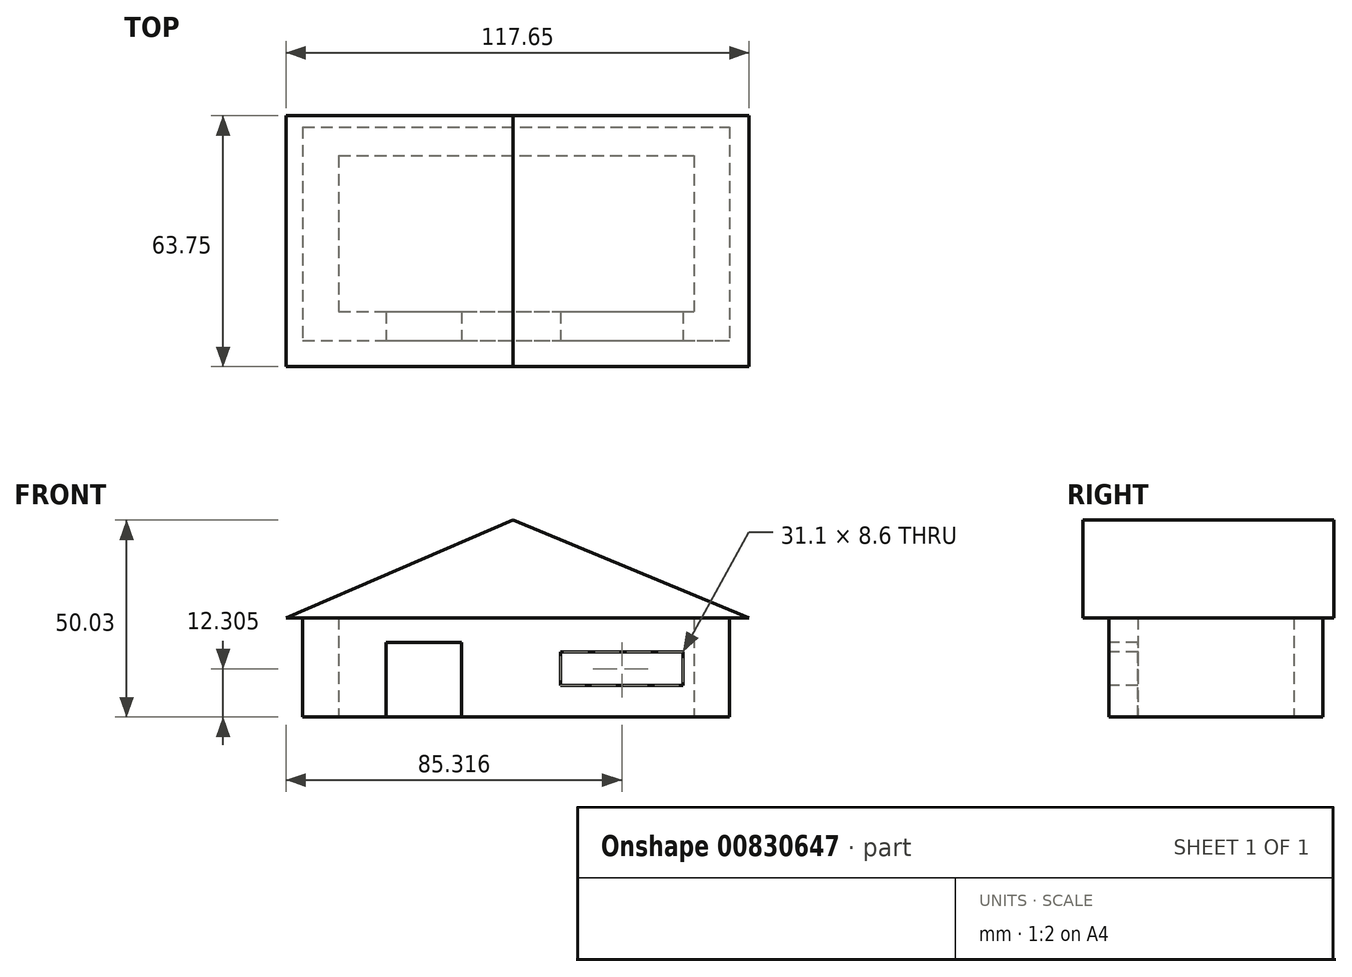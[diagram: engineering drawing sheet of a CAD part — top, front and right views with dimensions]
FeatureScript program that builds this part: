
annotation { "Feature Type Name" : "Feature", "Feature Type Description" : "" }
export const myFeature = defineFeature(function(context is Context, id is Id, definition is map)
    precondition{}
    {
        {
            var Q0;
            Q0=qCreatedBy(makeId("Top.planeOp"),FACE);
            var sketch = newSketch(context, id + "F0", { "sketchPlane" : qUnion([Q0])});
            skLineSegment(sketch, "E0.bottom", {"start": v(-45.13, 19.8) * mm, "end": v(45.13, 19.8) * mm});
            skLineSegment(sketch, "E0.top", {"start": v(-45.13, -19.8) * mm, "end": v(45.13, -19.8) * mm});
            skLineSegment(sketch, "E0.left", {"start": v(-45.13, 19.8) * mm, "end": v(-45.13, -19.8) * mm});
            skLineSegment(sketch, "E0.right", {"start": v(45.13, 19.8) * mm, "end": v(45.13, -19.8) * mm});
            skPoint(sketch, "E0.middle", {"position": v(0, 0) * mm});
            skLineSegment(sketch, "E1.bottom", {"start": v(-54.2, 27.15) * mm, "end": v(54.2, 27.15) * mm});
            skLineSegment(sketch, "E1.top", {"start": v(-54.2, -27.15) * mm, "end": v(54.2, -27.15) * mm});
            skLineSegment(sketch, "E1.left", {"start": v(-54.2, 27.15) * mm, "end": v(-54.2, -27.15) * mm});
            skLineSegment(sketch, "E1.right", {"start": v(54.2, 27.15) * mm, "end": v(54.2, -27.15) * mm});
            skLineSegment(sketch, "E2.bottom", {"start": v(-28.23, 27.15) * mm, "end": v(-10.51, 27.15) * mm});
            skLineSegment(sketch, "E2.top", {"start": v(-28.23, 19.8) * mm, "end": v(-10.51, 19.8) * mm});
            skLineSegment(sketch, "E2.left", {"start": v(-28.23, 27.15) * mm, "end": v(-28.23, 19.8) * mm});
            skLineSegment(sketch, "E2.right", {"start": v(-10.51, 27.15) * mm, "end": v(-10.51, 19.8) * mm});
            skSolve(sketch);
        }
        {
            var Q0;
            {var subQ2=sQuery(id+"F0.wireOp",EDGE,"E2.left");Q0=makeQuery(id+"F0.imprint","IMPRINT",FACE,{"disambiguationData":[TD([[makeQuery(id+"F0.imprint","IMPRINT",EDGE,{"derivedFrom":subQ2}),1.0]])]});}
            var Q1;
            Q1=makeQuery(id+"F0.imprint","IMPRINT",FACE,{"disambiguationData":[TD([[makeQuery(id+"F0.imprint","IMPRINT",EDGE,{"derivedFrom":sQuery(id+"F0.wireOp",EDGE,"E0.top")}),-1.0]])]});
            extrude(context, id + "F1", {"entities" : qUnion([Q0, Q1]), "depth" : 25.4 * mm, "offsetDistance" : 25.4 * mm});
        }
        {
            var Q0;
            Q0=makeQuery(id+"F1.opExtrude","SWEPT_FACE",FACE,{"disambiguationData":[OSD([sQuery(id+"F0.wireOp",EDGE,"E1.top")])]});
            var sketch = newSketch(context, id + "F2", { "sketchPlane" : qUnion([Q0])});
            skLineSegment(sketch, "E3.bottom", {"start": v(-33, 0) * mm, "end": v(-13.84, 0) * mm});
            skLineSegment(sketch, "E3.top", {"start": v(-33, 19) * mm, "end": v(-13.84, 19) * mm});
            skLineSegment(sketch, "E3.left", {"start": v(-33, 0) * mm, "end": v(-33, 19) * mm});
            skLineSegment(sketch, "E3.right", {"start": v(-13.84, 0) * mm, "end": v(-13.84, 19) * mm});
            skLineSegment(sketch, "E4.bottom", {"start": v(14, 19.1) * mm, "end": v(39.13, 19.1) * mm});
            skLineSegment(sketch, "E4.top", {"start": v(14, 8.94) * mm, "end": v(39.13, 8.94) * mm});
            skLineSegment(sketch, "E4.left", {"start": v(14, 19.1) * mm, "end": v(14, 8.94) * mm});
            skLineSegment(sketch, "E4.right", {"start": v(39.13, 19.1) * mm, "end": v(39.13, 8.94) * mm});
            skSolve(sketch);
        }
        {
            var Q0;
            Q0=makeQuery(id+"F2.imprint","IMPRINT",FACE,{"disambiguationData":[TD([[makeQuery(id+"F2.imprint","IMPRINT",EDGE,{"derivedFrom":sQuery(id+"F2.wireOp",EDGE,"E3.bottom")}),1.0]])]});
            extrude(context, id + "F3", {"entities" : qUnion([Q0]), "operationType" : NewBodyOperationType.REMOVE, "endBound" : BoundingType.UP_TO_NEXT, "oppositeDirection" : true, "depth" : 25.4 * mm, "offsetDistance" : 25.4 * mm});
        }
        {
            var Q0;
            Q0=makeQuery(id+"F1.opExtrude","SWEPT_FACE",FACE,{"disambiguationData":[OSD([sQuery(id+"F0.wireOp",EDGE,"E1.top")])]});
            var sketch = newSketch(context, id + "F4", { "sketchPlane" : qUnion([Q0])});
            skLineSegment(sketch, "E5.bottom", {"start": v(14.6, 17.68) * mm, "end": v(40.3, 17.68) * mm});
            skLineSegment(sketch, "E5.top", {"start": v(14.6, 7.44) * mm, "end": v(40.3, 7.44) * mm});
            skLineSegment(sketch, "E5.left", {"start": v(14.6, 17.68) * mm, "end": v(14.6, 7.44) * mm});
            skLineSegment(sketch, "E5.right", {"start": v(40.3, 17.68) * mm, "end": v(40.3, 7.44) * mm});
            skSolve(sketch);
        }
        {
            var Q0;
            Q0=makeQuery(id+"F4.imprint","IMPRINT",FACE,{"disambiguationData":[TD([[makeQuery(id+"F4.imprint","IMPRINT",EDGE,{"derivedFrom":sQuery(id+"F4.wireOp",EDGE,"E5.bottom")}),-1.0]])]});
            extrude(context, id + "F5", {"entities" : qUnion([Q0]), "operationType" : NewBodyOperationType.ADD, "endBound" : BoundingType.UP_TO_NEXT, "oppositeDirection" : true, "depth" : 25.4 * mm, "offsetDistance" : 25.4 * mm});
        }
        {
            var Q0;
            Q0=makeQuery(id+"F1.opExtrude","SWEPT_FACE",FACE,{"disambiguationData":[OSD([sQuery(id+"F0.wireOp",EDGE,"E1.top")])]});
            var sketch = newSketch(context, id + "F6", { "sketchPlane" : qUnion([Q0])});
            skLineSegment(sketch, "E6.bottom", {"start": v(11.3, 16.6) * mm, "end": v(42.4, 16.6) * mm});
            skLineSegment(sketch, "E6.top", {"start": v(11.3, 8) * mm, "end": v(42.4, 8) * mm});
            skLineSegment(sketch, "E6.left", {"start": v(11.3, 16.6) * mm, "end": v(11.3, 8) * mm});
            skLineSegment(sketch, "E6.right", {"start": v(42.4, 16.6) * mm, "end": v(42.4, 8) * mm});
            skSolve(sketch);
        }
        {
            var Q0;
            Q0=makeQuery(id+"F6.imprint","IMPRINT",FACE,{"disambiguationData":[TD([[makeQuery(id+"F6.imprint","IMPRINT",EDGE,{"derivedFrom":sQuery(id+"F6.wireOp",EDGE,"E6.bottom")}),-1.0]])]});
            extrude(context, id + "F7", {"entities" : qUnion([Q0]), "operationType" : NewBodyOperationType.REMOVE, "endBound" : BoundingType.UP_TO_NEXT, "oppositeDirection" : true, "depth" : 25.4 * mm, "offsetDistance" : 25.4 * mm});
        }
        {
            var Q0;
            Q0=qCreatedBy(makeId("Front.planeOp"),FACE);
            var sketch = newSketch(context, id + "F8", { "sketchPlane" : qUnion([Q0])});
            skLineSegment(sketch, "E7", {"start": v(-58.47, 25.24) * mm, "end": v(59.18, 25.24) * mm});
            skLineSegment(sketch, "E8", {"start": v(59.18, 25.24) * mm, "end": v(-0.8, 50.03) * mm});
            skLineSegment(sketch, "E9", {"start": v(-0.8, 50.03) * mm, "end": v(-58.47, 25.24) * mm});
            skSolve(sketch);
        }
        {
            var Q0;
            Q0=makeQuery(id+"F8.imprint","IMPRINT",FACE,{"disambiguationData":[TD([[makeQuery(id+"F8.imprint","IMPRINT",EDGE,{"derivedFrom":sQuery(id+"F8.wireOp",EDGE,"E7")}),1.0]])]});
            extrude(context, id + "F9", {"entities" : qUnion([Q0]), "operationType" : NewBodyOperationType.ADD, "depth" : 33.78 * mm, "offsetDistance" : 25.4 * mm, "hasSecondDirection" : true, "secondDirectionOppositeDirection" : true, "secondDirectionDepth" : 29.97 * mm});
        }
    });
